# Revit family: Hitachi_CSNET-Manager-LT_
name_source: partatom
category: Mechanical Equipment
revit_build: Autodesk Revit 2018 (Build: 20190510_1515(x64)
units: mm (PartAtom-declared; Revit-internal decimal feet)

## family parameters
Always vertical = Yes
Classification = None
Cut with Voids When Loaded = No
OmniClass Number = 23.75.65.14.17
OmniClass Title = Control and Monitoring Boards/Panels
Part Type = Normal
Room Calculation Point = No
Round Connector Dimension = Use Diameter
Shared = No
Work Plane-Based = Yes

## types (1)
- CSNET Manager 2T10
    BC_MODEL_ID = 350076
    BC_OBJECT_ID = 37744
    BC_OBJECT_VERSION = #5
    BC_VARIANT_ID = 230659
    Color = Noir
    Communication Type = Wired
    Default Elevation = 1219 mm
    Description = Commande centralisée avec interface tactile de 12 pouces
utilisant le logiciel CSNET Manager pour contrôler les unités
intérieures.
    ETIM Code = EC011603
    Electric Power = 60 W
    Manufacturer = Hitachi Air Conditioning Europe SAS
    Mass = 1.20 kg
    MasterFormat = Electric and Electronic Control System for HVAC
    Masterformat Code = 23 09 33
    Maximum Operating Temperature = 40 °C
    Maximum Voltage = 24 V
    Minimum Operating Temperature = 0 °C
    Minimum Voltage = 12 V
    Model = CSNET Manager LT
    Name = CSNET Manager LT
    Name BIM&CO = Panneau de contrôle
    Name ETIM = Accessoires pour climatiseur
    Nominal Current = 5 A
    Nominal Frequency Range = 50-60
    Number of Phases = 1
    OMNICLASS Table 23 Code  = 23-27 15 23 11
    Object type = Panneau de contrôle
    Omniclass = HVAC Main Control Panels
    Operating Humidity Range = 0~90%
    Overall Depth = 33 mm  [stored 0.108268 ft]
    Overall Height = 169 mm  [stored 0.554462 ft]
    Overall Width = 255 mm  [stored 0.836614 ft]
    Product Code = 7E512201
    Reference description = Commande centralisée avec interface tactile de 12 pouces
utilisant le logiciel CSNET Manager pour contrôler les unités
intérieures.
    Type Comments = Commande centralisée avec interface tactile de 12 pouces
utilisant le logiciel CSNET Manager pour contrôler les unités
intérieures.
    Uniformat = Contrôle électronique
    Uniformat code = D306002

note: [stored X ft] marks values corroborated as IEEE doubles in the binary element streams (Revit-internal decimal feet)

## geometry (parser evidence)
native form markers: Sweep x2
no freeform markers — native parametric forms only
